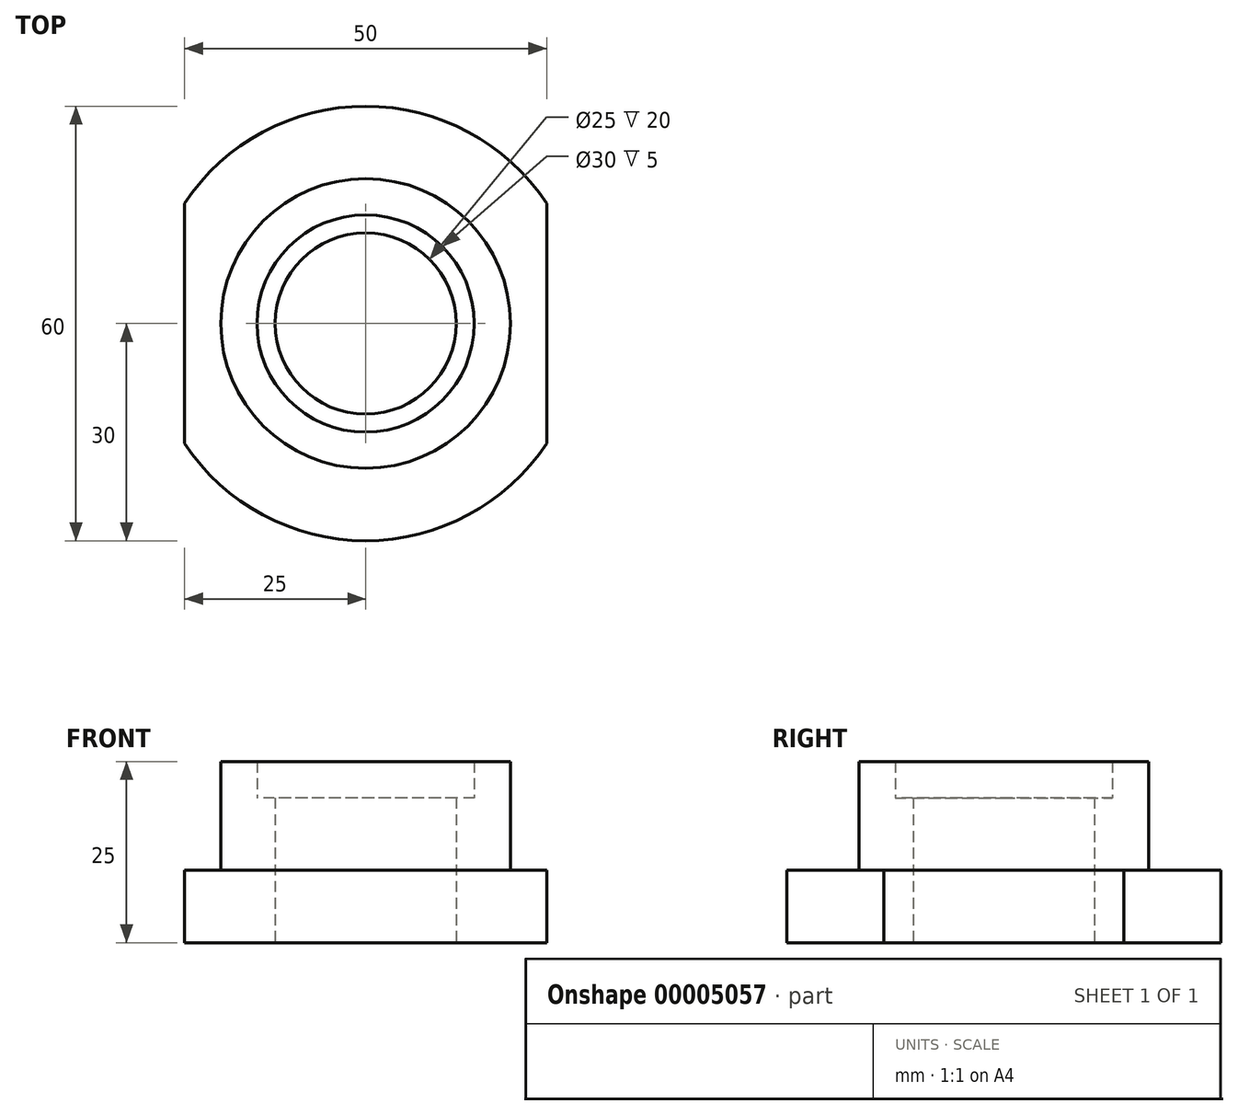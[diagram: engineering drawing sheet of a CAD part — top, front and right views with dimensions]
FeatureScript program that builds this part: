
annotation { "Feature Type Name" : "Feature", "Feature Type Description" : "" }
export const myFeature = defineFeature(function(context is Context, id is Id, definition is map)
    precondition{}
    {
        {
            var Q0;
            Q0=qCreatedBy(makeId("Top.planeOp"),FACE);
            var sketch = newSketch(context, id + "F0", { "sketchPlane" : qUnion([Q0])});
            skCircle(sketch, "E0", {"center": v(0, 0) * mm, "radius": 12.5 * mm});
            skCircle(sketch, "E1", {"center": v(0, 0) * mm, "radius": 15 * mm});
            skCircle(sketch, "E2", {"center": v(0, 0) * mm, "radius": 20 * mm});
            skCircle(sketch, "E3", {"center": v(0, 0) * mm, "radius": 30 * mm});
            skLineSegment(sketch, "E4.rect.bottom", {"start": v(25, -30) * mm, "end": v(-25, -30) * mm});
            skLineSegment(sketch, "E4.rect.top", {"start": v(25, 30) * mm, "end": v(-25, 30) * mm});
            skLineSegment(sketch, "E4.rect.left", {"start": v(25, -30) * mm, "end": v(25, 30) * mm});
            skLineSegment(sketch, "E4.rect.right", {"start": v(-25, -30) * mm, "end": v(-25, 30) * mm});
            skSolve(sketch);
        }
        {
            var Q0;
            Q0=makeQuery(id+"F0.imprint","IMPRINT",FACE,{"disambiguationData":[TD([[makeQuery(id+"F0.imprint","IMPRINT",EDGE,{"derivedFrom":sQuery(id+"F0.wireOp",EDGE,"E0")}),-1.0]])]});
            extrude(context, id + "F1", {"entities" : qUnion([Q0]), "depth" : 20 * mm});
        }
        {
            var Q0;
            Q0=makeQuery(id+"F0.imprint","IMPRINT",FACE,{"disambiguationData":[TD([[makeQuery(id+"F0.imprint","IMPRINT",EDGE,{"derivedFrom":sQuery(id+"F0.wireOp",EDGE,"E1")}),-1.0]])]});
            extrude(context, id + "F2", {"entities" : qUnion([Q0]), "operationType" : NewBodyOperationType.ADD, "depth" : 25 * mm});
        }
        {
            var Q0;
            Q0=makeQuery(id+"F0.imprint","IMPRINT",FACE,{"disambiguationData":[TD([[makeQuery(id+"F0.imprint","IMPRINT",EDGE,{"derivedFrom":sQuery(id+"F0.wireOp",EDGE,"E2")}),-1.0]])]});
            extrude(context, id + "F3", {"entities" : qUnion([Q0]), "operationType" : NewBodyOperationType.ADD, "depth" : 10 * mm});
        }
    });
